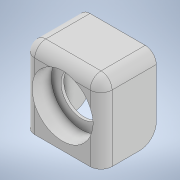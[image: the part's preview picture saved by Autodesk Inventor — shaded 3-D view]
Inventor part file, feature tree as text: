
AUTODESK INVENTOR PART (.ipt)
format: ipt  version: 2021 (Build 250183000, 183)  size: 168,448 bytes
history: native  units: mm
features: extrude x3, sketch x3, fillet x2, projected_geometry x2
ambient origin geometry x8: Origin, YZ Plane, XZ Plane, XY Plane, X Axis, Y Axis, Z Axis, Center Point
bodies: Solid1 (feature_tree)
feature tree (10):
  extrude  "Extrusion1"  Depth=20.0mm
  extrude  "Extrusion2"  Depth=4.0mm
  extrude  "Extrusion3"  Depth=4.0mm
  fillet  "Fillet1"  Radius=1.0mm
  fillet  "Fillet2"  Radius=22.0mm
  sketch  "Sketch1"  dims[d0=15.0mm d1=20.0mm]
  sketch  "Sketch2"  dims[d2=20.0mm d3=4.0mm]
  projected_geometry  "Projected Loop1"
  sketch  "Sketch3"  dims[d4=4.0mm d5=4.0mm d6=1.0mm d7=0.0mm d8=22.0mm d9=4.0mm d10=7.0mm d11=0.0mm d12=4.0mm d13=12.0mm d14=0.0mm d15=6.0mm d16=4.0mm]
  projected_geometry  "Projected Loop2"
